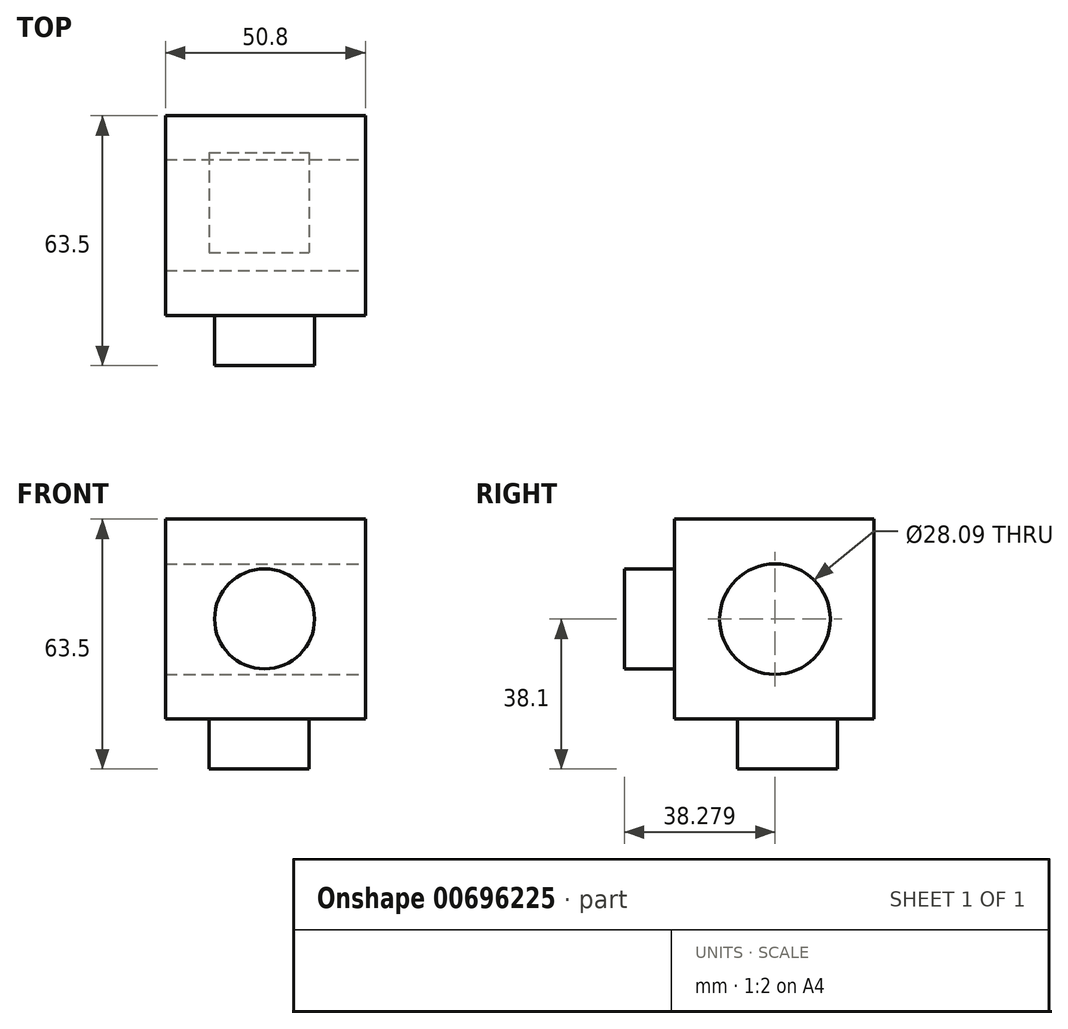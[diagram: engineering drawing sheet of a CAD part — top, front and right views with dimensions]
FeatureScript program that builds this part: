
annotation { "Feature Type Name" : "Feature", "Feature Type Description" : "" }
export const myFeature = defineFeature(function(context is Context, id is Id, definition is map)
    precondition{}
    {
        {
            var Q0;
            Q0=qCreatedBy(makeId("Front.planeOp"),FACE);
            var sketch = newSketch(context, id + "F0", { "sketchPlane" : qUnion([Q0])});
            skLineSegment(sketch, "E0.bottom", {"start": v(0, 0) * mm, "end": v(50.8, 0) * mm});
            skLineSegment(sketch, "E0.top", {"start": v(0, 50.8) * mm, "end": v(50.8, 50.8) * mm});
            skLineSegment(sketch, "E0.left", {"start": v(0, 0) * mm, "end": v(0, 50.8) * mm});
            skLineSegment(sketch, "E0.right", {"start": v(50.8, 0) * mm, "end": v(50.8, 50.8) * mm});
            skSolve(sketch);
        }
        {
            var Q0;
            Q0 = qSketchRegion(id + "F0", true);
            extrude(context, id + "F1", {"entities" : qUnion([Q0]), "depth" : 50.8 * mm, "offsetDistance" : 25.4 * mm});
        }
        {
            var Q0;
            Q0=makeQuery(id+"F1.opExtrude","CAP_FACE",FACE,{"disambiguationData":[OSD([sQuery(id+"F0.wireOp",EDGE,"E0.bottom"),sQuery(id+"F0.wireOp",EDGE,"E0.top"),sQuery(id+"F0.wireOp",EDGE,"E0.left"),sQuery(id+"F0.wireOp",EDGE,"E0.right")])],"isStart":false});
            var sketch = newSketch(context, id + "F2", { "sketchPlane" : qUnion([Q0])});
            skCircle(sketch, "E1", {"center": v(25.18, 25.47) * mm, "radius": 12.7 * mm});
            skSolve(sketch);
        }
        {
            var Q0;
            Q0 = qSketchRegion(id + "F2", true);
            extrude(context, id + "F3", {"entities" : qUnion([Q0]), "operationType" : NewBodyOperationType.ADD, "depth" : 12.7 * mm, "offsetDistance" : 25.4 * mm});
        }
        {
            var Q0;
            Q0=makeQuery(id+"F1.opExtrude","SWEPT_FACE",FACE,{"disambiguationData":[OSD([sQuery(id+"F0.wireOp",EDGE,"E0.right")])]});
            var sketch = newSketch(context, id + "F4", { "sketchPlane" : qUnion([Q0])});
            skCircle(sketch, "E2", {"center": v(-25.22, 25.4) * mm, "radius": 14.05 * mm});
            skPoint(sketch, "E2.centerSnap0", {"position": v(0, 25.4) * mm});
            skSolve(sketch);
        }
        {
            var Q0;
            Q0 = qSketchRegion(id + "F4", true);
            extrude(context, id + "F5", {"entities" : qUnion([Q0]), "operationType" : NewBodyOperationType.REMOVE, "oppositeDirection" : true, "depth" : 50.8 * mm, "offsetDistance" : 25.4 * mm});
        }
        {
            var Q0;
            Q0=makeQuery(id+"F1.opExtrude","SWEPT_FACE",FACE,{"disambiguationData":[OSD([sQuery(id+"F0.wireOp",EDGE,"E0.bottom")])]});
            var sketch = newSketch(context, id + "F6", { "sketchPlane" : qUnion([Q0])});
            skLineSegment(sketch, "E3.bottom", {"start": v(11.05, 9.35) * mm, "end": v(36.45, 9.35) * mm});
            skLineSegment(sketch, "E3.top", {"start": v(11.05, 34.75) * mm, "end": v(36.45, 34.75) * mm});
            skLineSegment(sketch, "E3.left", {"start": v(11.05, 9.35) * mm, "end": v(11.05, 34.75) * mm});
            skLineSegment(sketch, "E3.right", {"start": v(36.45, 9.35) * mm, "end": v(36.45, 34.75) * mm});
            skSolve(sketch);
        }
        {
            var Q0;
            Q0 = qSketchRegion(id + "F6", true);
            extrude(context, id + "F7", {"entities" : qUnion([Q0]), "operationType" : NewBodyOperationType.ADD, "depth" : 12.7 * mm, "offsetDistance" : 25.4 * mm});
        }
    });
